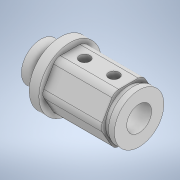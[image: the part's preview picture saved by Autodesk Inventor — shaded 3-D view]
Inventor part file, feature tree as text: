
AUTODESK INVENTOR PART (.ipt)
format: ipt  version: 2020 (Build 240168000, 168)  size: 406,528 bytes
history: native  units: mm
features: sketch x15, extrude x13, fillet x4
ambient origin geometry x8: Origin, YZ Plane, XZ Plane, XY Plane, X Axis, Y Axis, Z Axis, Center Point
bodies: Solid1 (feature_tree)
feature tree (32):
  extrude  "Extrusion1"  Depth=1.28mm TaperAngle=0.0deg
  extrude  "Extrusion2"  Depth=7.5mm
  extrude  "Extrusion3"  Depth=1.5mm TaperAngle=0.0deg
  extrude  "Extrusion4"  Depth=0.75mm
  fillet  "Fillet1"  Radius=2.705mm
  fillet  "Fillet2"  Radius=6.5mm
  sketch  "Sketch5"  dims[d15=6.4mm d16=11.75mm d17=0.0mm]
  extrude  "Extrusion5"  Depth=11.75mm TaperAngle=0.0deg
  sketch  "Sketch7"  dims[d21=2.0mm d22=10.0mm d23=0.0mm d24=7.5mm d25=0.0mm]
  sketch  "Sketch8"  dims[d26=2.0mm d27=25.0mm d28=0.0mm]
  extrude  "Extrusion6"  Depth=5.0mm TaperAngle=0.0deg
  extrude  "Extrusion7"  Depth=10.0mm TaperAngle=0.0deg
  fillet  "Fillet3"  Radius=7.5mm
  extrude  "Extrusion8"  Depth=2.0mm TaperAngle=0.0deg
  extrude  "Extrusion9"  Depth=5.0mm
  fillet  "Fillet4"  Radius=5.0mm
  extrude  "Extrusion10"  Depth=2.5mm TaperAngle=0.0deg
  extrude  "Extrusion11"  Depth=5.0mm TaperAngle=0.0deg
  extrude  "Extrusion12"  [1 undecoded]
  extrude  "Extrusion13"  [1 undecoded]
  sketch  "Sketch1"  dims[d0=15.197mm d1=1.28mm d2=0.0mm]
  sketch  "Sketch2"  dims[d3=7.5mm d4=0.0mm d5=11.854mm]
  sketch  "Sketch3"  dims[d6=1.22mm d7=0.0mm d8=1.5mm d9=0.0mm]
  sketch  "Sketch4"  dims[d10=0.75mm d11=0.75mm d12=2.705mm d13=6.5mm d14=0.0mm]
  sketch  "Sketch6"  dims[d18=8.4mm d19=5.0mm d20=0.0mm]
  sketch  "Sketch9"  dims[d29=3.75mm d30=2.705mm d31=5.0mm d32=0.0mm]
  sketch  "Sketch10"  dims[d33=16.0mm d34=2.5mm d35=0.0mm]
  sketch  "Sketch11"  dims[d36=10.0mm d37=5.0mm d38=0.0mm]
  sketch  "Sketch12"
  sketch  "Sketch13"
  sketch  "Sketch14"
  sketch  "Sketch15"
note: 2 required parameter values undecoded (feature->parameter linkage not recoverable at this tier; creation-order binding heuristic only, values carry confidence <= 0.55)
